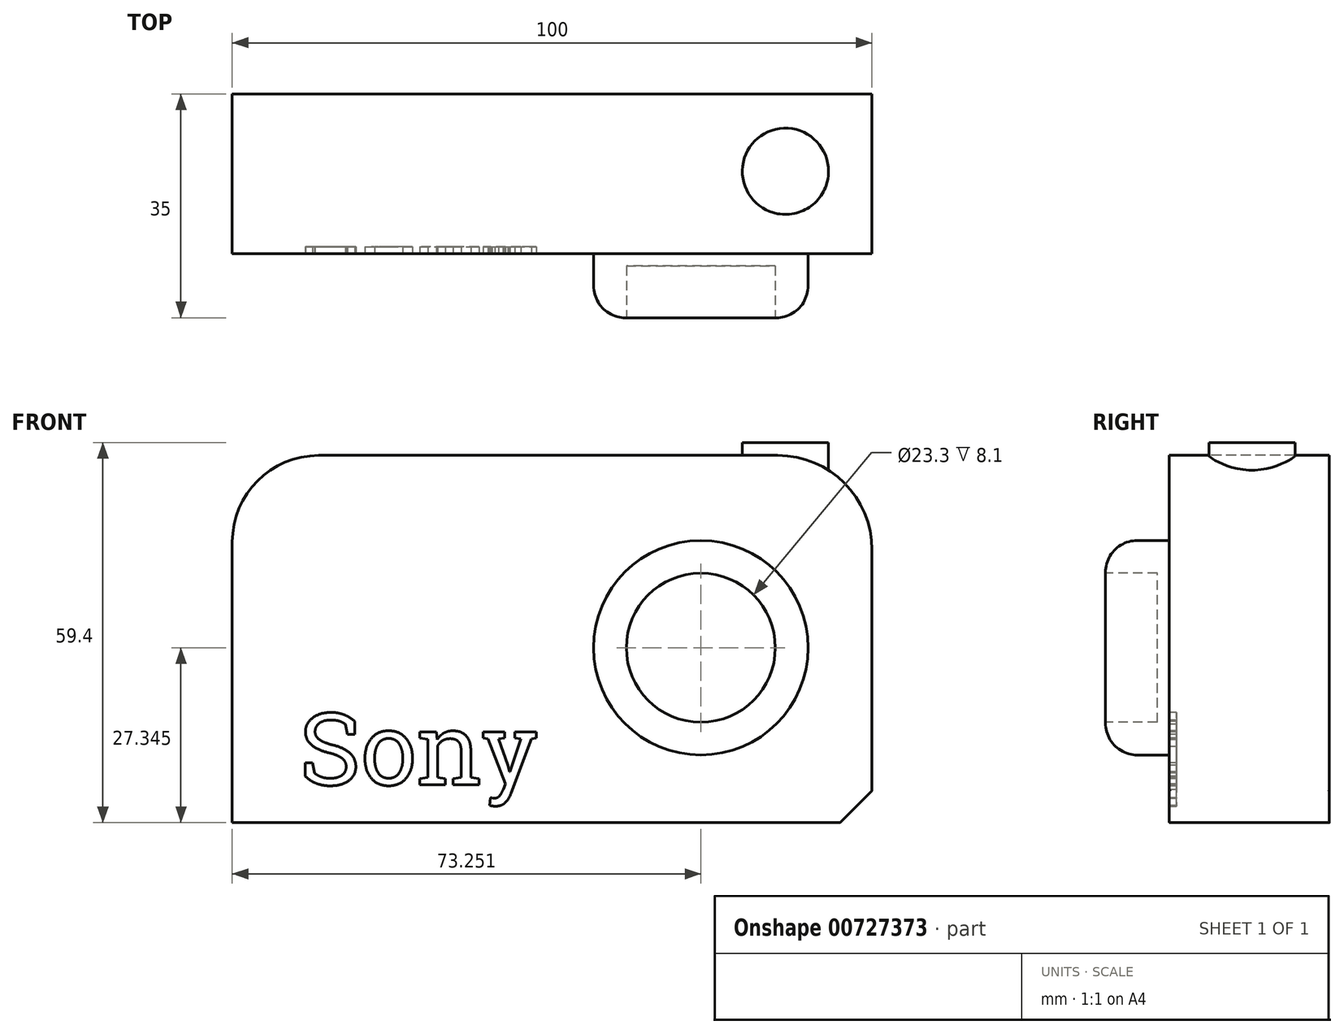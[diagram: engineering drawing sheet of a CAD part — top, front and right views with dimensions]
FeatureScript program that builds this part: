
annotation { "Feature Type Name" : "Feature", "Feature Type Description" : "" }
export const myFeature = defineFeature(function(context is Context, id is Id, definition is map)
    precondition{}
    {
        {
            var Q0;
            Q0=qCreatedBy(makeId("Top.planeOp"),FACE);
            var sketch = newSketch(context, id + "F0", { "sketchPlane" : qUnion([Q0])});
            skLineSegment(sketch, "E0.bottom", {"start": v(-108.64, -19.32) * mm, "end": v(-8.64, -19.32) * mm});
            skLineSegment(sketch, "E0.top", {"start": v(-108.64, -44.32) * mm, "end": v(-8.64, -44.32) * mm});
            skLineSegment(sketch, "E0.left", {"start": v(-108.64, -19.32) * mm, "end": v(-108.64, -44.32) * mm});
            skLineSegment(sketch, "E0.right", {"start": v(-8.64, -19.32) * mm, "end": v(-8.64, -44.32) * mm});
            skSolve(sketch);
        }
        {
            var Q0;
            Q0=qSketchRegion(id+"F0",true);
            extrude(context, id + "F1", {"entities" : qUnion([Q0]), "depth" : 57.4 * mm, "offsetDistance" : 25 * mm});
        }
        {
            var Q0;
            Q0=makeQuery(id+"F1.opExtrude","SWEPT_FACE",FACE,{"disambiguationData":[OSD([sQuery(id+"F0.wireOp",EDGE,"E0.top")])]});
            var sketch = newSketch(context, id + "F2", { "sketchPlane" : qUnion([Q0])});
            skCircle(sketch, "E1", {"center": v(-35.39, 27.34) * mm, "radius": 16.76 * mm});
            skSolve(sketch);
        }
        {
            var Q0;
            Q0=qSketchRegion(id+"F2",true);
            extrude(context, id + "F3", {"entities" : qUnion([Q0]), "operationType" : NewBodyOperationType.ADD, "depth" : 10 * mm, "offsetDistance" : 25 * mm});
        }
        {
            var Q0;
            Q0=makeQuery(id+"F3.opExtrude","CAP_FACE",FACE,{"disambiguationData":[OSD([sQuery(id+"F2.wireOp",EDGE,"E1")])],"isStart":false});
            var sketch = newSketch(context, id + "F4", { "sketchPlane" : qUnion([Q0])});
            skCircle(sketch, "E2", {"center": v(-35.39, 27.34) * mm, "radius": 11.65 * mm});
            skSolve(sketch);
        }
        {
            var Q0;
            Q0=qSketchRegion(id+"F4",true);
            extrude(context, id + "F5", {"entities" : qUnion([Q0]), "operationType" : NewBodyOperationType.REMOVE, "oppositeDirection" : true, "depth" : 8.1 * mm, "offsetDistance" : 25 * mm});
        }
        {
            var Q0;
            Q0=makeQuery(id+"F1.opExtrude","CAP_EDGE",EDGE,{"disambiguationData":[OSD([sQuery(id+"F0.wireOp",EDGE,"E0.left")])],"isStart":false});
            fillet(context, id + "F6", {"entities" : qUnion([Q0]), "radius" : 13.52 * mm, "tangentPropagation" : true, "allowEdgeOverflow" : false});
        }
        {
            var Q0;
            Q0=makeQuery(id+"F1.opExtrude","CAP_EDGE",EDGE,{"disambiguationData":[OSD([sQuery(id+"F0.wireOp",EDGE,"E0.right")])],"isStart":true});
            chamfer(context, id + "F7", {"entities" : qUnion([Q0]), "width" : 5 * mm, "tangentPropagation" : true});
        }
        {
            var Q0;
            Q0=makeQuery(id+"F3.opExtrude","CAP_EDGE",EDGE,{"disambiguationData":[OSD([sQuery(id+"F2.wireOp",EDGE,"E1")])],"isStart":false});
            fillet(context, id + "F8", {"entities" : qUnion([Q0]), "radius" : 5 * mm, "tangentPropagation" : true, "allowEdgeOverflow" : false});
        }
        {
            var Q0;
            Q0=makeQuery(id+"F1.opExtrude","CAP_FACE",FACE,{"disambiguationData":[OSD([sQuery(id+"F0.wireOp",EDGE,"E0.bottom"),sQuery(id+"F0.wireOp",EDGE,"E0.top"),sQuery(id+"F0.wireOp",EDGE,"E0.left"),sQuery(id+"F0.wireOp",EDGE,"E0.right")])],"isStart":false});
            var sketch = newSketch(context, id + "F9", { "sketchPlane" : qUnion([Q0])});
            skCircle(sketch, "E3", {"center": v(-22.17, -31.42) * mm, "radius": 6.73 * mm});
            skSolve(sketch);
        }
        {
            var Q0;
            Q0=qSketchRegion(id+"F9",true);
            extrude(context, id + "F10", {"entities" : qUnion([Q0]), "operationType" : NewBodyOperationType.ADD, "depth" : 2 * mm, "offsetDistance" : 25 * mm});
        }
        {
            var Q0;
            Q0=makeQuery(id+"F1.opExtrude","SWEPT_FACE",FACE,{"disambiguationData":[OSD([sQuery(id+"F0.wireOp",EDGE,"E0.top")])]});
            var sketch = newSketch(context, id + "F11", { "sketchPlane" : qUnion([Q0])});
            skText(sketch, "E4", { "text": "Sony", "fontName": "RobotoSlab-Regular.ttf"});
            const initialGuessF11  = {"E4": [-0.09814, 0.00592, 1, 0, 0.0113]};
            skSetInitialGuess(sketch, initialGuessF11);
            skSolve(sketch);
        }
        {
            var Q0;
            Q0=qSketchRegion(id+"F11",true);
            extrude(context, id + "F12", {"entities" : qUnion([Q0]), "operationType" : NewBodyOperationType.REMOVE, "oppositeDirection" : true, "depth" : 1.1 * mm, "offsetDistance" : 25 * mm});
        }
        {
            var Q0;
            Q0=makeQuery(id+"F1.opExtrude","CAP_EDGE",EDGE,{"disambiguationData":[OSD([sQuery(id+"F0.wireOp",EDGE,"E0.right")])],"isStart":false});
            fillet(context, id + "F13", {"entities" : qUnion([Q0]), "radius" : 14.73 * mm, "tangentPropagation" : true, "allowEdgeOverflow" : false});
        }
        {
            var Q0;
            Q0=makeQuery(id+"F7.opChamfer","BLEND_FACE",FACE,{"disambiguationData":[OSD([sQuery(id+"F0.wireOp",EDGE,"E0.right")])]});
            fillet(context, id + "F14", {"entities" : qUnion([Q0]), "radius" : 0.12 * mm, "tangentPropagation" : true, "allowEdgeOverflow" : false});
        }
    });
